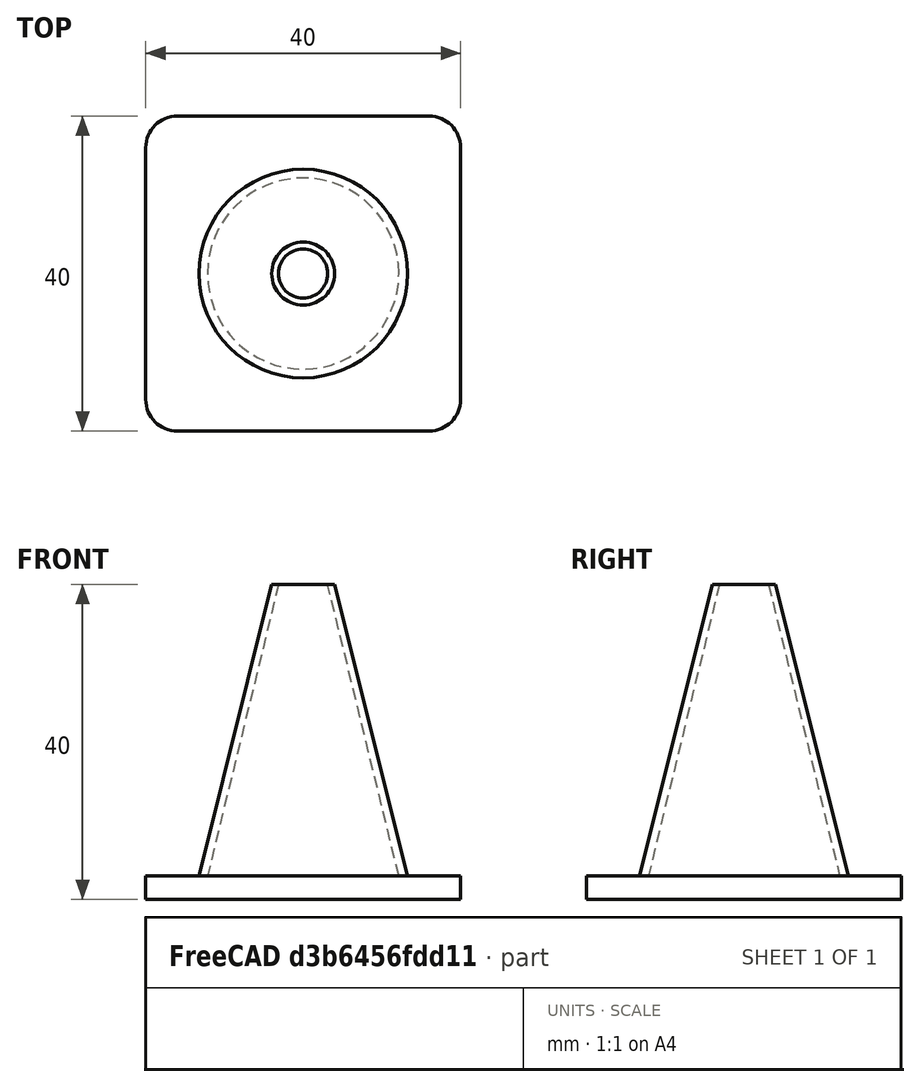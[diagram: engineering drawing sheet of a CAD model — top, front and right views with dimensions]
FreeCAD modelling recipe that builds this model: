
FCSTD DOCUMENT  (FreeCAD 1.0R39319 (Git))
Label: ojt1_t14r02_cone
License: All rights reserved
LicenseURL: https://en.wikipedia.org/wiki/All_rights_reserved
objects: Part::Cone×2, Part::Box×1, Part::Fillet×1, Part::Cut×1, Part::MultiFuse×1
note: 6 computed .brp shape members not serialized (recipe doc carries the construction recipe); baked Part::Feature solids carry a one-line shape summary decoded from their .brp

FEATURE [Part::Box] Box  label="Cub"
  AttacherType = Attacher::AttachEngine3D
  Height = 3
  Length = 40
  Width = 40
FEATURE [Part::Fillet] Fillet
  Base = -> Box
  EdgeLinks = -> Box [Edge1,Edge3,Edge5,Edge7]
  Edges = 4 edges r=4: [Edge1,Edge3,Edge5,Edge7]
FEATURE [Part::Cone] Cone  label="Con"
  Angle = 360
  AttacherType = Attacher::AttachEngine3D
  Height = 40
  Placement = pos=(20,20,0) rot=(0,0,1;0rad)
  Radius1 = 14
  Radius2 = 4
FEATURE [Part::Cone] Cone001  label="Con001"
  Angle = 360
  AttacherType = Attacher::AttachEngine3D
  Height = 41
  Placement = pos=(20,20,-0.5) rot=(0,0,1;0rad)
  Radius1 = 13
  Radius2 = 3
FEATURE [Part::Cut] Cut
  Base = -> Cone
  Refine = true
  Tool = -> Cone001
FEATURE [Part::MultiFuse] Fusion
  Refine = true
  Shapes = -> [Fillet,Cut]
